# Revit family: Telegraph Reader LED_ 8587,8588,8589
name_source: partatom
category: Lighting Fixtures
revit_build: Autodesk Revit 2018 (Build: 20170223_1515(x64)
units: mm (PartAtom-declared; Revit-internal decimal feet)

## family parameters
Always vertical = Yes
Cut with Voids When Loaded = No
Host = Wall
Light Source = Yes
OmniClass Number = 23.80.70.00
OmniClass Title = Lighting
Part Type = Normal
Room Calculation Point = No
Round Connector Dimension = Use Diameter
Shared = No

## types (2) — shared parameters
Color Filter = 16777215
Dimming Lamp Color Temperature Shift = <None>
Driver Required = No
Light Source Symbol Length = 3048 mm  [stored 10 ft]
Manufacturer = Astro Lighting Ltd
Tilt Angle = 60.00°
URL = www.astrolighting.com

## per-type parameters (varying)
| type | ADA compliant | Apparent Load | Dimmable | Dimming Method | Driver Included | Efficacy (lm/w) | Electrical Class | Lamp | Length of Cable Supplied | Light Source Fixed | Location rating | Main Finish | Main Material | Power (Watts) | Product Code | Product Location | Product Name | Product SKU | Spot Beam Angle | Spot Field Angle | Wattage Comments |
| CE | To be advised | 13 VA | Non Dimming | Not Applicable | Yes | 36.34 | 1 | LED -2W - Luxeon TX L1T2-27803 | Not Applicable | Adjustable | IP20 | Matt Nickel | Metal - Zinc | 4.1 | 8588 | Indoor | Telegraph Reader LED | 1404014 | 17.00° | 34.00° | Not Applicable |
| ETL | NO | 0 VA |  |  |  |  | 0 |  |  |  | DAMP |  | Metal - Steel |  | 1234 | Bathroom |  | 1234001 | 30.00° | 90.00° |  |

note: [stored X ft] marks values corroborated as IEEE doubles in the binary element streams (Revit-internal decimal feet)

## geometry (parser evidence)
native form markers: Sweep x2
no freeform markers — native parametric forms only
